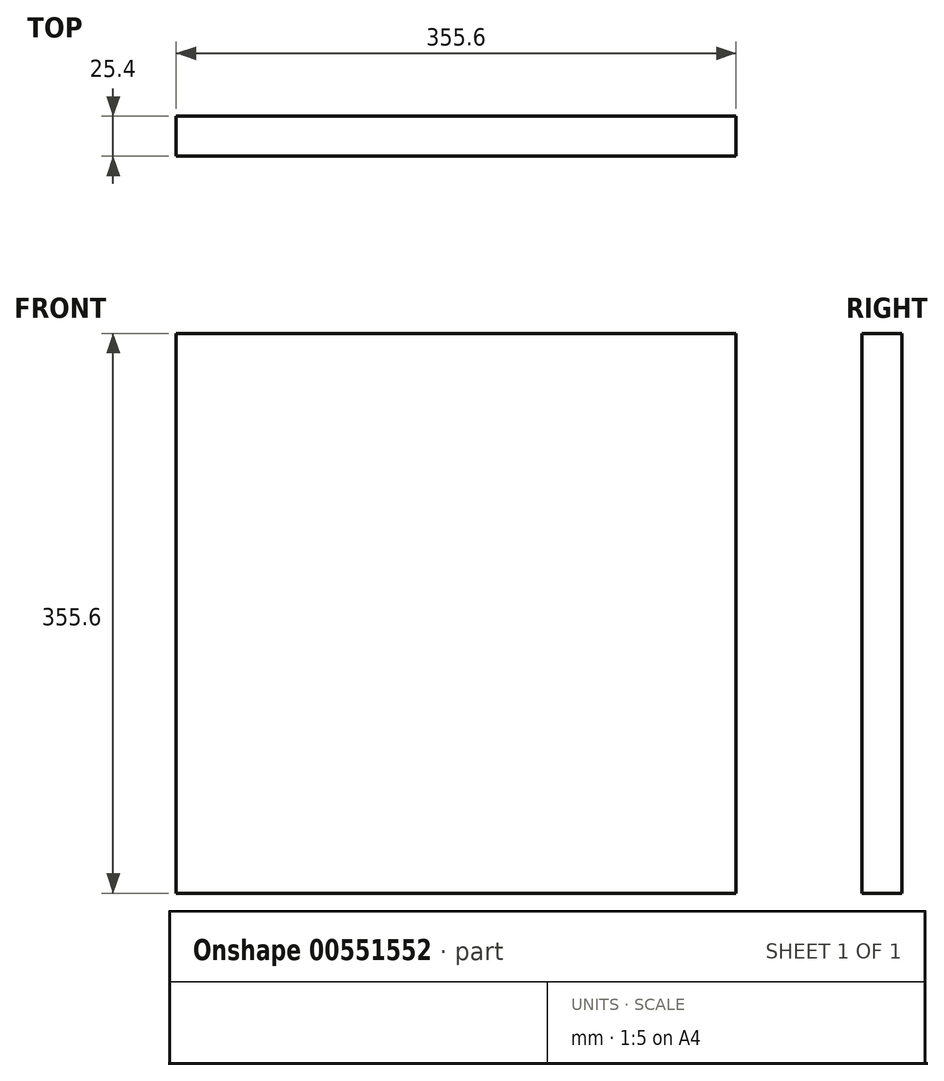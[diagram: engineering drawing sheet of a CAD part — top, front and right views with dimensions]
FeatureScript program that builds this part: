
annotation { "Feature Type Name" : "Feature", "Feature Type Description" : "" }
export const myFeature = defineFeature(function(context is Context, id is Id, definition is map)
    precondition{}
    {
        {
            var Q0;
            Q0=qCreatedBy(makeId("Front.planeOp"),FACE);
            var sketch = newSketch(context, id + "F0", { "sketchPlane" : qUnion([Q0])});
            skLineSegment(sketch, "E0.bottom", {"start": v(0, 0) * mm, "end": v(355.6, 0) * mm});
            skLineSegment(sketch, "E0.top", {"start": v(0, 355.6) * mm, "end": v(355.6, 355.6) * mm});
            skLineSegment(sketch, "E0.left", {"start": v(0, 0) * mm, "end": v(0, 355.6) * mm});
            skLineSegment(sketch, "E0.right", {"start": v(355.6, 0) * mm, "end": v(355.6, 355.6) * mm});
            skPoint(sketch, "E1.oppositeSnap0", {"position": v(177.8, 355.6) * mm});
            skLineSegment(sketch, "E1.bottom", {"start": v(0, 0) * mm, "end": v(177.8, 0) * mm});
            skLineSegment(sketch, "E1.top", {"start": v(0, 304.8) * mm, "end": v(177.8, 304.8) * mm});
            skLineSegment(sketch, "E1.left", {"start": v(0, 0) * mm, "end": v(0, 304.8) * mm});
            skLineSegment(sketch, "E1.right", {"start": v(177.8, 0) * mm, "end": v(177.8, 304.8) * mm});
            skLineSegment(sketch, "E2", {"start": v(177.8, 152.4) * mm, "end": v(0, 152.4) * mm});
            skSolve(sketch);
        }
        {
            var Q0;
            Q0 = qSketchRegion(id + "F0", true);
            extrude(context, id + "F1", {"entities" : qUnion([Q0]), "depth" : 25.4 * mm, "offsetDistance" : 25.4 * mm});
        }
    });
